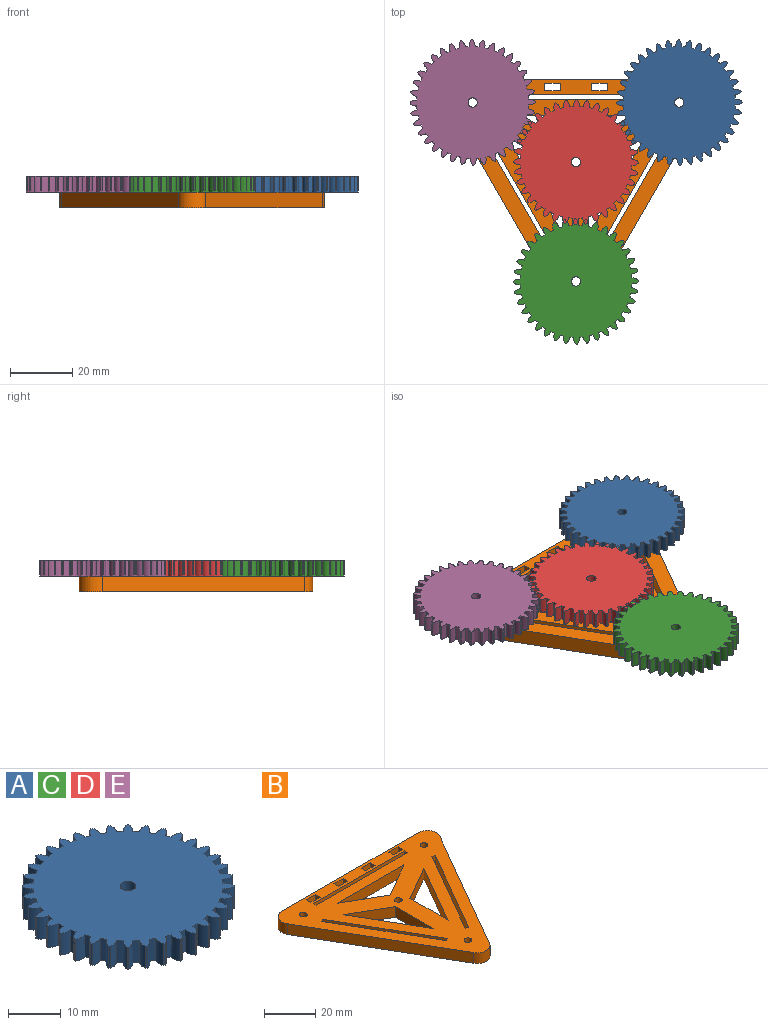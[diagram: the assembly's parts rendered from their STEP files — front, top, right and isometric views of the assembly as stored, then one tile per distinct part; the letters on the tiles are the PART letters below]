
ASSEMBLY  parts=5 mates=4
PART A: 147 faces, bbox 40.1x40.1x5.1 mm
  f0: plane 5.08x0.35mm, normal (-1,-0.09,0), area 1.8mm2, adj f1,f144,f145,f146
  f1: cylinder r=2.95mm len=5.08mm, axis (0,0,-1), area 11.9mm2, adj f0,f2,f145,f146
  f2: cylinder r=17.99mm len=5.08mm, axis (0,0,-1), area 6.4mm2, adj f1,f3,f145,f146
  f3: cylinder r=2.95mm len=5.08mm, axis (0,0,-1), area 11.9mm2, adj f2,f4,f145,f146
  f4: plane 5.08x0.34mm, normal (-0.97,-0.26,0), area 1.8mm2, adj f3,f5,f145,f146
  f5: cylinder r=2.95mm len=5.08mm, axis (0,0,-1), area 11.9mm2, adj f4,f6,f145,f146
  f6: cylinder r=17.99mm len=5.08mm, axis (0,0,-1), area 6.4mm2, adj f5,f7,f145,f146
  f7: cylinder r=2.95mm len=5.08mm, axis (0,0,-1), area 11.9mm2, adj f6,f8,f145,f146
  f8: plane 5.08x0.32mm, normal (-0.91,-0.42,0), area 1.8mm2, adj f7,f9,f145,f146
  f9: cylinder r=2.95mm len=5.08mm, axis (0,0,-1), area 11.9mm2, adj f8,f10,f145,f146
  f10: cylinder r=17.99mm len=5.08mm, axis (0,0,-1), area 6.4mm2, adj f9,f11,f145,f146
  f11: cylinder r=2.95mm len=5.08mm, axis (0,0,-1), area 11.9mm2, adj f10,f12,f145,f146
  f12: plane 5.08x0.29mm, normal (-0.82,-0.57,0), area 1.8mm2, adj f11,f13,f145,f146
  f13: cylinder r=2.95mm len=5.08mm, axis (0,0,-1), area 11.9mm2, adj f12,f14,f145,f146
  f14: cylinder r=17.99mm len=5.08mm, axis (0,0,-1), area 6.4mm2, adj f13,f15,f145,f146
  f15: cylinder r=2.95mm len=5.08mm, axis (0,0,-1), area 11.9mm2, adj f14,f16,f145,f146
  f16: plane 5.08x0.25mm, normal (-0.71,-0.71,0), area 1.8mm2, adj f15,f17,f145,f146
  f17: cylinder r=2.95mm len=5.08mm, axis (0,0,-1), area 11.9mm2, adj f16,f18,f145,f146
  f18: cylinder r=17.99mm len=5.08mm, axis (0,0,-1), area 6.4mm2, adj f17,f19,f145,f146
  f19: cylinder r=2.95mm len=5.08mm, axis (0,0,-1), area 11.9mm2, adj f18,f20,f145,f146
  f20: plane 5.08x0.29mm, normal (-0.57,-0.82,0), area 1.8mm2, adj f19,f21,f145,f146
  f21: cylinder r=2.95mm len=5.08mm, axis (0,0,-1), area 11.9mm2, adj f20,f22,f145,f146
  f22: cylinder r=17.99mm len=5.08mm, axis (0,0,-1), area 6.4mm2, adj f21,f23,f145,f146
  f23: cylinder r=2.95mm len=5.08mm, axis (0,0,-1), area 11.9mm2, adj f22,f24,f145,f146
  f24: plane 5.08x0.32mm, normal (-0.42,-0.91,0), area 1.8mm2, adj f23,f25,f145,f146
  f25: cylinder r=2.95mm len=5.08mm, axis (0,0,-1), area 11.9mm2, adj f24,f26,f145,f146
  f26: cylinder r=17.99mm len=5.08mm, axis (0,0,-1), area 6.4mm2, adj f25,f27,f145,f146
  f27: cylinder r=2.95mm len=5.08mm, axis (0,0,-1), area 11.9mm2, adj f26,f28,f145,f146
  f28: plane 5.08x0.34mm, normal (-0.26,-0.97,0), area 1.8mm2, adj f27,f29,f145,f146
  f29: cylinder r=2.95mm len=5.08mm, axis (0,0,-1), area 11.9mm2, adj f28,f30,f145,f146
  f30: cylinder r=17.99mm len=5.08mm, axis (0,0,-1), area 6.4mm2, adj f29,f31,f145,f146
  f31: cylinder r=2.95mm len=5.08mm, axis (0,0,-1), area 11.9mm2, adj f30,f32,f145,f146
  f32: plane 5.08x0.35mm, normal (-0.09,-1,0), area 1.8mm2, adj f31,f33,f145,f146
  f33: cylinder r=2.95mm len=5.08mm, axis (0,0,-1), area 11.9mm2, adj f32,f34,f145,f146
  f34: cylinder r=17.99mm len=5.08mm, axis (0,0,-1), area 6.4mm2, adj f33,f35,f145,f146
  f35: cylinder r=2.95mm len=5.08mm, axis (0,0,-1), area 11.9mm2, adj f34,f36,f145,f146
  f36: plane 5.08x0.35mm, normal (0.09,-1,0), area 1.8mm2, adj f35,f37,f145,f146
  f37: cylinder r=2.95mm len=5.08mm, axis (0,0,-1), area 11.9mm2, adj f36,f38,f145,f146
  f38: cylinder r=17.99mm len=5.08mm, axis (0,0,-1), area 6.4mm2, adj f37,f39,f145,f146
  f39: cylinder r=2.95mm len=5.08mm, axis (0,0,-1), area 11.9mm2, adj f38,f40,f145,f146
  f40: plane 5.08x0.34mm, normal (0.26,-0.97,0), area 1.8mm2, adj f39,f41,f145,f146
  f41: cylinder r=2.95mm len=5.08mm, axis (0,0,-1), area 11.9mm2, adj f40,f42,f145,f146
  f42: cylinder r=17.99mm len=5.08mm, axis (0,0,-1), area 6.4mm2, adj f41,f43,f145,f146
  f43: cylinder r=2.95mm len=5.08mm, axis (0,0,-1), area 11.9mm2, adj f42,f44,f145,f146
  f44: plane 5.08x0.32mm, normal (0.42,-0.91,0), area 1.8mm2, adj f43,f45,f145,f146
  f45: cylinder r=2.95mm len=5.08mm, axis (0,0,-1), area 11.9mm2, adj f44,f46,f145,f146
  f46: cylinder r=17.99mm len=5.08mm, axis (0,0,-1), area 6.4mm2, adj f45,f47,f145,f146
  f47: cylinder r=2.95mm len=5.08mm, axis (0,0,-1), area 11.9mm2, adj f46,f48,f145,f146
  f48: plane 5.08x0.29mm, normal (0.57,-0.82,0), area 1.8mm2, adj f47,f49,f145,f146
  f49: cylinder r=2.95mm len=5.08mm, axis (0,0,-1), area 11.9mm2, adj f48,f50,f145,f146
  f50: cylinder r=17.99mm len=5.08mm, axis (0,0,-1), area 6.4mm2, adj f49,f51,f145,f146
  f51: cylinder r=2.95mm len=5.08mm, axis (0,0,-1), area 11.9mm2, adj f50,f52,f145,f146
  f52: plane 5.08x0.25mm, normal (0.71,-0.71,0), area 1.8mm2, adj f51,f53,f145,f146
  f53: cylinder r=2.95mm len=5.08mm, axis (0,0,-1), area 11.9mm2, adj f52,f54,f145,f146
  f54: cylinder r=17.99mm len=5.08mm, axis (0,0,-1), area 6.4mm2, adj f53,f55,f145,f146
  f55: cylinder r=2.95mm len=5.08mm, axis (0,0,-1), area 11.9mm2, adj f54,f56,f145,f146
  f56: plane 5.08x0.29mm, normal (0.82,-0.57,0), area 1.8mm2, adj f55,f57,f145,f146
  f57: cylinder r=2.95mm len=5.08mm, axis (0,0,-1), area 11.9mm2, adj f56,f58,f145,f146
  f58: cylinder r=17.99mm len=5.08mm, axis (0,0,-1), area 6.4mm2, adj f57,f59,f145,f146
  f59: cylinder r=2.95mm len=5.08mm, axis (0,0,-1), area 11.9mm2, adj f58,f60,f145,f146
  f60: plane 5.08x0.32mm, normal (0.91,-0.42,0), area 1.8mm2, adj f59,f61,f145,f146
  f61: cylinder r=2.95mm len=5.08mm, axis (0,0,-1), area 11.9mm2, adj f60,f62,f145,f146
  f62: cylinder r=17.99mm len=5.08mm, axis (0,0,-1), area 6.4mm2, adj f61,f63,f145,f146
  f63: cylinder r=2.95mm len=5.08mm, axis (0,0,-1), area 11.9mm2, adj f62,f64,f145,f146
  f64: plane 5.08x0.34mm, normal (0.97,-0.26,0), area 1.8mm2, adj f63,f65,f145,f146
  f65: cylinder r=2.95mm len=5.08mm, axis (0,0,-1), area 11.9mm2, adj f64,f66,f145,f146
  f66: cylinder r=17.99mm len=5.08mm, axis (0,0,-1), area 6.4mm2, adj f65,f67,f145,f146
  f67: cylinder r=2.95mm len=5.08mm, axis (0,0,-1), area 11.9mm2, adj f66,f68,f145,f146
  f68: plane 5.08x0.35mm, normal (1,-0.09,0), area 1.8mm2, adj f67,f69,f145,f146
  f69: cylinder r=2.95mm len=5.08mm, axis (0,0,-1), area 11.9mm2, adj f68,f70,f145,f146
  f70: cylinder r=17.99mm len=5.08mm, axis (0,0,-1), area 6.4mm2, adj f69,f71,f145,f146
  f71: cylinder r=2.95mm len=5.08mm, axis (0,0,-1), area 11.9mm2, adj f70,f72,f145,f146
  f72: plane 5.08x0.35mm, normal (1,0.09,0), area 1.8mm2, adj f71,f73,f145,f146
  f73: cylinder r=2.95mm len=5.08mm, axis (0,0,-1), area 11.9mm2, adj f72,f74,f145,f146
  f74: cylinder r=17.99mm len=5.08mm, axis (0,0,-1), area 6.4mm2, adj f73,f75,f145,f146
  f75: cylinder r=2.95mm len=5.08mm, axis (0,0,-1), area 11.9mm2, adj f74,f76,f145,f146
  f76: plane 5.08x0.34mm, normal (0.97,0.26,0), area 1.8mm2, adj f75,f77,f145,f146
  f77: cylinder r=2.95mm len=5.08mm, axis (0,0,-1), area 11.9mm2, adj f76,f78,f145,f146
  f78: cylinder r=17.99mm len=5.08mm, axis (0,0,-1), area 6.4mm2, adj f77,f79,f145,f146
  f79: cylinder r=2.95mm len=5.08mm, axis (0,0,-1), area 11.9mm2, adj f78,f80,f145,f146
  f80: plane 5.08x0.32mm, normal (0.91,0.42,0), area 1.8mm2, adj f79,f81,f145,f146
  f81: cylinder r=2.95mm len=5.08mm, axis (0,0,-1), area 11.9mm2, adj f80,f82,f145,f146
  f82: cylinder r=17.99mm len=5.08mm, axis (0,0,-1), area 6.4mm2, adj f81,f83,f145,f146
  f83: cylinder r=2.95mm len=5.08mm, axis (0,0,-1), area 11.9mm2, adj f82,f84,f145,f146
  f84: plane 5.08x0.29mm, normal (0.82,0.57,0), area 1.8mm2, adj f83,f85,f145,f146
  f85: cylinder r=2.95mm len=5.08mm, axis (0,0,-1), area 11.9mm2, adj f84,f86,f145,f146
  f86: cylinder r=17.99mm len=5.08mm, axis (0,0,-1), area 6.4mm2, adj f85,f87,f145,f146
  f87: cylinder r=2.95mm len=5.08mm, axis (0,0,-1), area 11.9mm2, adj f86,f88,f145,f146
  f88: plane 5.08x0.25mm, normal (0.71,0.71,0), area 1.8mm2, adj f87,f89,f145,f146
  f89: cylinder r=2.95mm len=5.08mm, axis (0,0,-1), area 11.9mm2, adj f88,f90,f145,f146
  f90: cylinder r=17.99mm len=5.08mm, axis (0,0,-1), area 6.4mm2, adj f89,f91,f145,f146
  f91: cylinder r=2.95mm len=5.08mm, axis (0,0,-1), area 11.9mm2, adj f90,f92,f145,f146
  f92: plane 5.08x0.29mm, normal (0.57,0.82,0), area 1.8mm2, adj f91,f93,f145,f146
  f93: cylinder r=2.95mm len=5.08mm, axis (0,0,-1), area 11.9mm2, adj f92,f94,f145,f146
  f94: cylinder r=17.99mm len=5.08mm, axis (0,0,-1), area 6.4mm2, adj f93,f95,f145,f146
  f95: cylinder r=2.95mm len=5.08mm, axis (0,0,-1), area 11.9mm2, adj f94,f96,f145,f146
  f96: plane 5.08x0.32mm, normal (0.42,0.91,0), area 1.8mm2, adj f95,f97,f145,f146
  f97: cylinder r=2.95mm len=5.08mm, axis (0,0,-1), area 11.9mm2, adj f96,f98,f145,f146
  f98: cylinder r=17.99mm len=5.08mm, axis (0,0,-1), area 6.4mm2, adj f97,f99,f145,f146
  f99: cylinder r=2.95mm len=5.08mm, axis (0,0,-1), area 11.9mm2, adj f98,f100,f145,f146
  f100: plane 5.08x0.34mm, normal (0.26,0.97,0), area 1.8mm2, adj f99,f101,f145,f146
  f101: cylinder r=2.95mm len=5.08mm, axis (0,0,-1), area 11.9mm2, adj f100,f102,f145,f146
  f102: cylinder r=17.99mm len=5.08mm, axis (0,0,-1), area 6.4mm2, adj f101,f103,f145,f146
  f103: cylinder r=2.95mm len=5.08mm, axis (0,0,-1), area 11.9mm2, adj f102,f104,f145,f146
  f104: plane 5.08x0.35mm, normal (0.09,1,0), area 1.8mm2, adj f103,f105,f145,f146
  f105: cylinder r=2.95mm len=5.08mm, axis (0,0,-1), area 11.9mm2, adj f104,f106,f145,f146
  f106: cylinder r=17.99mm len=5.08mm, axis (0,0,-1), area 6.4mm2, adj f105,f107,f145,f146
  f107: cylinder r=2.95mm len=5.08mm, axis (0,0,-1), area 11.9mm2, adj f106,f108,f145,f146
  f108: plane 5.08x0.35mm, normal (-0.09,1,0), area 1.8mm2, adj f107,f109,f145,f146
  f109: cylinder r=2.95mm len=5.08mm, axis (0,0,-1), area 11.9mm2, adj f108,f110,f145,f146
  f110: cylinder r=17.99mm len=5.08mm, axis (0,0,-1), area 6.4mm2, adj f109,f111,f145,f146
  f111: cylinder r=2.95mm len=5.08mm, axis (0,0,-1), area 11.9mm2, adj f110,f112,f145,f146
  f112: plane 5.08x0.34mm, normal (-0.26,0.97,0), area 1.8mm2, adj f111,f113,f145,f146
  f113: cylinder r=2.95mm len=5.08mm, axis (0,0,-1), area 11.9mm2, adj f112,f114,f145,f146
  f114: cylinder r=17.99mm len=5.08mm, axis (0,0,-1), area 6.4mm2, adj f113,f115,f145,f146
  f115: cylinder r=2.95mm len=5.08mm, axis (0,0,-1), area 11.9mm2, adj f114,f116,f145,f146
  f116: plane 5.08x0.32mm, normal (-0.42,0.91,0), area 1.8mm2, adj f115,f117,f145,f146
  f117: cylinder r=2.95mm len=5.08mm, axis (0,0,-1), area 11.9mm2, adj f116,f118,f145,f146
  f118: cylinder r=17.99mm len=5.08mm, axis (0,0,-1), area 6.4mm2, adj f117,f119,f145,f146
  f119: cylinder r=2.95mm len=5.08mm, axis (0,0,-1), area 11.9mm2, adj f118,f120,f145,f146
  f120: plane 5.08x0.29mm, normal (-0.57,0.82,0), area 1.8mm2, adj f119,f121,f145,f146
  f121: cylinder r=2.95mm len=5.08mm, axis (0,0,-1), area 11.9mm2, adj f120,f122,f145,f146
  f122: cylinder r=17.99mm len=5.08mm, axis (0,0,-1), area 6.4mm2, adj f121,f123,f145,f146
  f123: cylinder r=2.95mm len=5.08mm, axis (0,0,-1), area 11.9mm2, adj f122,f124,f145,f146
  f124: plane 5.08x0.25mm, normal (-0.71,0.71,0), area 1.8mm2, adj f123,f125,f145,f146
  f125: cylinder r=2.95mm len=5.08mm, axis (0,0,-1), area 11.9mm2, adj f124,f126,f145,f146
  f126: cylinder r=17.99mm len=5.08mm, axis (0,0,-1), area 6.4mm2, adj f125,f127,f145,f146
  f127: cylinder r=2.95mm len=5.08mm, axis (0,0,-1), area 11.9mm2, adj f126,f128,f145,f146
  f128: plane 5.08x0.29mm, normal (-0.82,0.57,0), area 1.8mm2, adj f127,f129,f145,f146
  f129: cylinder r=2.95mm len=5.08mm, axis (0,0,-1), area 11.9mm2, adj f128,f130,f145,f146
  f130: cylinder r=17.99mm len=5.08mm, axis (0,0,-1), area 6.4mm2, adj f129,f131,f145,f146
  f131: cylinder r=2.95mm len=5.08mm, axis (0,0,-1), area 11.9mm2, adj f130,f132,f145,f146
  f132: plane 5.08x0.32mm, normal (-0.91,0.42,0), area 1.8mm2, adj f131,f133,f145,f146
  f133: cylinder r=2.95mm len=5.08mm, axis (0,0,-1), area 11.9mm2, adj f132,f134,f145,f146
  f134: cylinder r=17.99mm len=5.08mm, axis (0,0,-1), area 6.4mm2, adj f133,f135,f145,f146
  f135: cylinder r=2.95mm len=5.08mm, axis (0,0,-1), area 11.9mm2, adj f134,f136,f145,f146
  f136: plane 5.08x0.34mm, normal (-0.97,0.26,0), area 1.8mm2, adj f135,f137,f145,f146
  f137: cylinder r=2.95mm len=5.08mm, axis (0,0,-1), area 11.9mm2, adj f136,f138,f145,f146
  f138: cylinder r=17.99mm len=5.08mm, axis (0,0,-1), area 6.4mm2, adj f137,f139,f145,f146
  f139: cylinder r=2.95mm len=5.08mm, axis (0,0,-1), area 11.9mm2, adj f138,f140,f145,f146
  f140: plane 5.08x0.35mm, normal (-1,0.09,0), area 1.8mm2, adj f139,f141,f145,f146
  f141: cylinder r=2.95mm len=5.08mm, axis (0,0,-1), area 11.9mm2, adj f140,f142,f145,f146
  f142: cylinder r=17.99mm len=5.08mm, axis (0,0,-1), area 6.4mm2, adj f141,f144,f145,f146
  f143: cylinder r=1.5mm len=5.08mm, axis (0,0,-1), area 47.9mm2, adj f145,f146
  f144: cylinder r=2.95mm len=5.08mm, axis (0,0,-1), area 11.9mm2, adj f0,f142,f145,f146
  f145: plane 40.08x40.08mm, normal (0,0,1), area 1119.3mm2, adj f0,f1,f2,f3,f4,f5,f6,f7
  f146: plane 40.08x40.08mm, normal (0,0,-1), area 1119.3mm2, adj f0,f1,f2,f3,f4,f5,f6,f7
PART B: 49 faces, bbox 84.9x74.9x5.1 mm
  f0: plane 84.91x74.88mm, normal (0,0,1), area 2754.5mm2, adj f2,f3,f4,f5,f6,f7,f8,f9
  f1: plane 84.91x74.88mm, normal (0,0,-1), area 2754.5mm2, adj f2,f3,f4,f5,f6,f7,f8,f9
  f2: plane 18.2x10.51mm, normal (0.5,0.87,0), area 106.7mm2, adj f0,f1,f3,f10
  f3: plane 36.39x5.08mm, normal (0,-1,0), area 184.9mm2, adj f0,f1,f2,f10
  f4: plane 74.91x5.08mm, normal (0,1,0), area 380.5mm2, adj f0,f1,f18,f20
  f5: plane 64.88x37.46mm, normal (-0.87,-0.5,0), area 380.5mm2, adj f0,f1,f18,f19
  f6: plane 31.52x18.2mm, normal (0.87,0.5,0), area 184.9mm2, adj f0,f1,f7,f15
  f7: plane 18.2x10.51mm, normal (-0.5,-0.87,0), area 106.7mm2, adj f0,f1,f6,f15
  f8: plane 18.2x10.51mm, normal (0.5,-0.87,0), area 106.7mm2, adj f0,f1,f9,f16
  f9: plane 31.52x18.2mm, normal (-0.87,0.5,0), area 184.9mm2, adj f0,f1,f8,f16
  f10: plane 18.2x10.51mm, normal (-0.5,0.87,0), area 106.7mm2, adj f0,f1,f2,f3
  f11: cylinder r=1.5mm len=5.08mm, axis (0,0,-1), area 47.9mm2, adj f0,f1
  f12: cylinder r=1.5mm len=5.08mm, axis (0,0,-1), area 47.9mm2, adj f0,f1
  f13: cylinder r=1.5mm len=5.08mm, axis (0,0,-1), area 47.9mm2, adj f0,f1
  f14: plane 64.88x37.46mm, normal (0.87,-0.5,0), area 380.5mm2, adj f0,f1,f19,f20
  f15: plane 21.01x5.08mm, normal (-1,0,0), area 106.7mm2, adj f0,f1,f6,f7
  f16: plane 21.01x5.08mm, normal (1,0,0), area 106.7mm2, adj f0,f1,f8,f9
  f17: cylinder r=1.5mm len=5.08mm, axis (0,0,-1), area 47.9mm2, adj f0,f1
  f18: cylinder r=5mm len=7.5mm, axis (0,0,-1), area 53.2mm2, adj f0,f1,f4,f5
  f19: cylinder r=5mm len=8.66mm, axis (0,0,1), area 53.2mm2, adj f0,f1,f5,f14
  f20: cylinder r=5mm len=7.5mm, axis (0,0,1), area 53.2mm2, adj f0,f1,f4,f14
  f21: plane 50x5.08mm, normal (0,1,0), area 254mm2, adj f0,f1,f22,f24
  f22: plane 5.08x1.5mm, normal (-1,0,0), area 7.6mm2, adj f0,f1,f21,f23
  f23: plane 50x5.08mm, normal (0,-1,0), area 254mm2, adj f0,f1,f22,f24
  f24: plane 5.08x1.5mm, normal (1,0,0), area 7.6mm2, adj f0,f1,f21,f23
  f25: plane 5.08x5.08mm, normal (0,-1,0), area 25.8mm2, adj f0,f1,f26,f28
  f26: plane 5.08x2.5mm, normal (1,0,0), area 12.7mm2, adj f0,f1,f25,f27
  f27: plane 5.08x5.08mm, normal (0,1,0), area 25.8mm2, adj f0,f1,f26,f28
  f28: plane 5.08x2.5mm, normal (-1,0,0), area 12.7mm2, adj f0,f1,f25,f27
  f29: plane 5.08x2.5mm, normal (-1,0,0), area 12.7mm2, adj f0,f1,f30,f32
  f30: plane 5.08x5.08mm, normal (0,-1,0), area 25.8mm2, adj f0,f1,f29,f31
  f31: plane 5.08x2.5mm, normal (1,0,0), area 12.7mm2, adj f0,f1,f30,f32
  f32: plane 5.08x5.08mm, normal (0,1,0), area 25.8mm2, adj f0,f1,f29,f31
  f33: plane 5.08x2.5mm, normal (1,0,0), area 12.7mm2, adj f0,f1,f34,f36
  f34: plane 5.08x5.08mm, normal (0,1,0), area 25.8mm2, adj f0,f1,f33,f35
  f35: plane 5.08x2.5mm, normal (-1,0,0), area 12.7mm2, adj f0,f1,f34,f36
  f36: plane 5.08x5.08mm, normal (0,-1,0), area 25.8mm2, adj f0,f1,f33,f35
  f37: plane 5.08x2.5mm, normal (1,0,0), area 12.7mm2, adj f0,f1,f38,f40
  f38: plane 5.08x5.08mm, normal (0,1,0), area 25.8mm2, adj f0,f1,f37,f39
  f39: plane 5.08x2.5mm, normal (-1,0,0), area 12.7mm2, adj f0,f1,f38,f40
  f40: plane 5.08x5.08mm, normal (0,-1,0), area 25.8mm2, adj f0,f1,f37,f39
  f41: plane 5.08x1.3mm, normal (0.5,0.87,0), area 7.6mm2, adj f0,f1,f42,f44
  f42: plane 43.3x25mm, normal (-0.87,0.5,0), area 254mm2, adj f0,f1,f41,f43
  f43: plane 5.08x1.3mm, normal (-0.5,-0.87,0), area 7.6mm2, adj f0,f1,f42,f44
  f44: plane 43.3x25mm, normal (0.87,-0.5,0), area 254mm2, adj f0,f1,f41,f43
  f45: plane 5.08x1.3mm, normal (0.5,-0.87,0), area 7.6mm2, adj f0,f1,f46,f48
  f46: plane 43.3x25mm, normal (0.87,0.5,0), area 254mm2, adj f0,f1,f45,f47
  f47: plane 5.08x1.3mm, normal (-0.5,0.87,0), area 7.6mm2, adj f0,f1,f46,f48
  f48: plane 43.3x25mm, normal (-0.87,-0.5,0), area 254mm2, adj f0,f1,f45,f47
PART C: same geometry as A
PART D: same geometry as A
PART E: same geometry as A
PLACE A rot(axis=(0.98,-0.21,0),180deg) t=(84.14,57.08,2.68)mm
PLACE B t=(51.02,-13.54,-7.48)mm fixed
PLACE C rot(axis=(0.98,-0.21,0),180deg) t=(51.02,-0.3,2.68)mm
PLACE D rot(axis=(-0.98,-0.21,0),180deg) t=(51.02,37.95,2.68)mm
PLACE E rot(axis=(0.98,-0.21,0),180deg) t=(17.89,57.08,2.68)mm
MATE revolute E.f138 <-> B.f13  axis (0,0,-1) through (17.89,57.08,-2.4)mm
MATE revolute A.f143 <-> B.f11  axis (0,0,-1) through (84.14,57.08,-2.4)mm
MATE revolute C.f143 <-> B.f12  axis (0,0,-1) through (51.02,-0.3,-2.4)mm
MATE revolute D.f143 <-> B.f17  axis (0,0,-1) through (51.02,37.95,-2.4)mm
